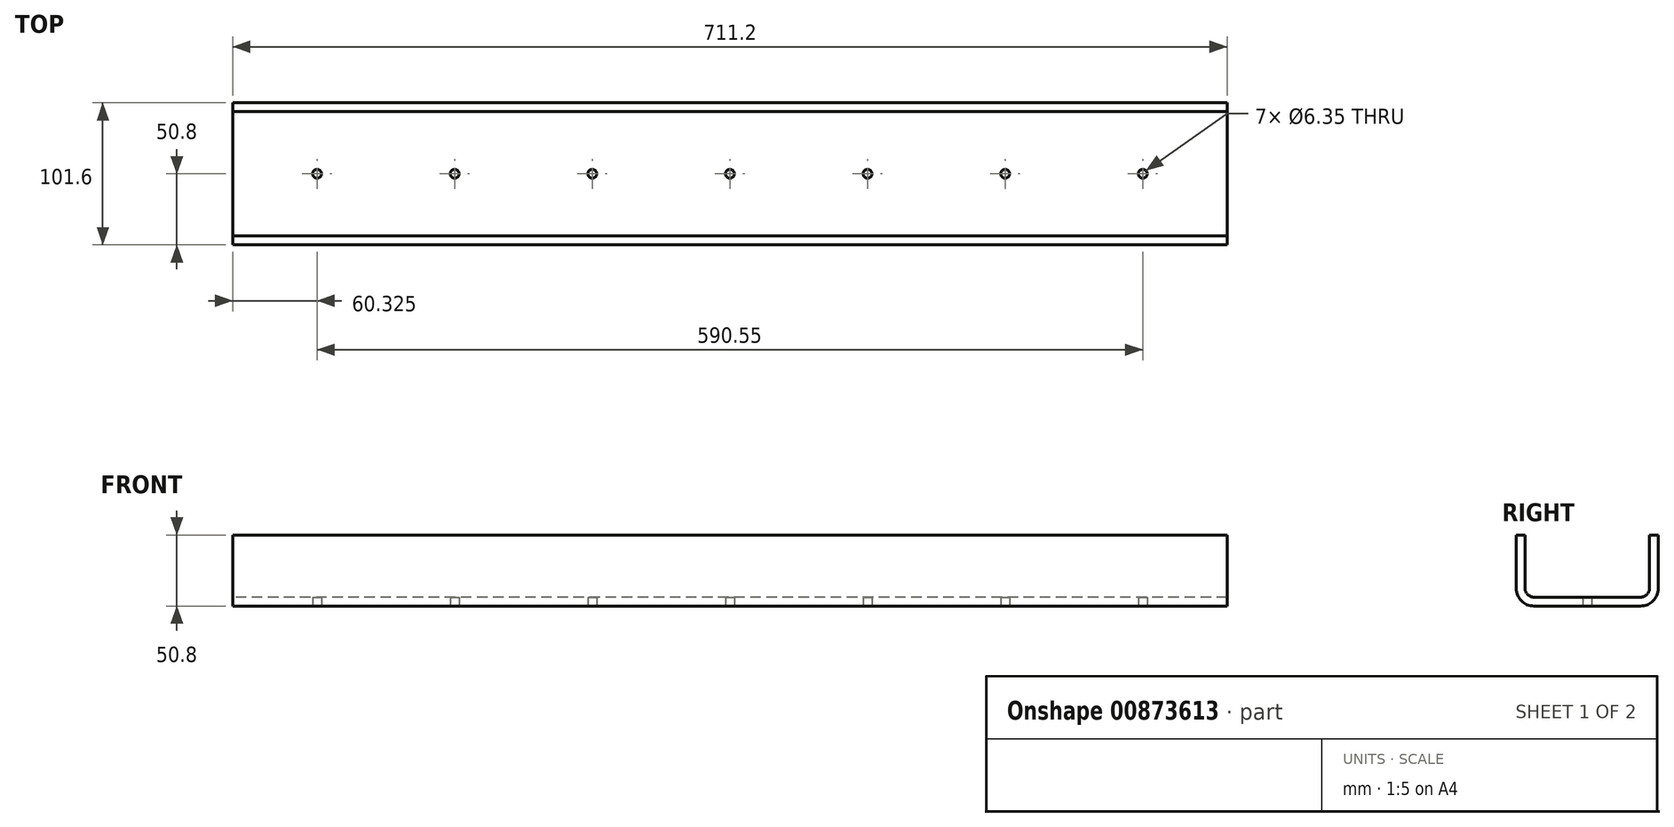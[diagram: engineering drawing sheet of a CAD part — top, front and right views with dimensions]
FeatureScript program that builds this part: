
annotation { "Feature Type Name" : "Feature", "Feature Type Description" : "" }
export const myFeature = defineFeature(function(context is Context, id is Id, definition is map)
    precondition{}
    {
        {
            var Q0;
            Q0=qCreatedBy(makeId("Right.planeOp"),FACE);
            var sketch = newSketch(context, id + "F0", { "sketchPlane" : qUnion([Q0])});
            skLineSegment(sketch, "E0.top", {"start": v(38.1, -25.4) * mm, "end": v(-38.1, -25.4) * mm});
            skLineSegment(sketch, "E0.left", {"start": v(50.8, 25.4) * mm, "end": v(50.8, -12.7) * mm});
            skLineSegment(sketch, "E0.right", {"start": v(-50.8, 25.4) * mm, "end": v(-50.8, -12.7) * mm});
            skPoint(sketch, "E0.middle", {"position": v(0, 0) * mm});
            skPoint(sketch, "E1.visualSharp", {"position": v(-50.8, -25.4) * mm});
            skArc(sketch, "E1.filletArc", {"start": v(-50.8, -12.7) * mm, "mid": v(-47.08, -21.68) * mm, "end": v(-38.1, -25.4) * mm});
            skPoint(sketch, "E2.visualSharp", {"position": v(50.8, -25.4) * mm});
            skArc(sketch, "E2.filletArc", {"start": v(38.1, -25.4) * mm, "mid": v(47.08, -21.68) * mm, "end": v(50.8, -12.7) * mm});
            skLineSegment(sketch, "E3.0", {"start": v(-44.45, 25.4) * mm, "end": v(-44.45, -12.7) * mm});
            skLineSegment(sketch, "E3.1", {"start": v(38.1, -19.05) * mm, "end": v(-38.1, -19.05) * mm});
            skLineSegment(sketch, "E3.2", {"start": v(44.45, 25.4) * mm, "end": v(44.45, -12.7) * mm});
            skLineSegment(sketch, "E4", {"start": v(-50.8, 25.4) * mm, "end": v(-44.45, 25.4) * mm});
            skLineSegment(sketch, "E5", {"start": v(44.45, 25.4) * mm, "end": v(50.8, 25.4) * mm});
            skPoint(sketch, "E6.visualSharp", {"position": v(-44.45, -19.05) * mm});
            skArc(sketch, "E6.filletArc", {"start": v(-44.45, -12.7) * mm, "mid": v(-42.6, -17.2) * mm, "end": v(-38.1, -19.05) * mm});
            skPoint(sketch, "E7.visualSharp", {"position": v(44.45, -19.05) * mm});
            skArc(sketch, "E7.filletArc", {"start": v(38.1, -19.05) * mm, "mid": v(42.6, -17.2) * mm, "end": v(44.45, -12.7) * mm});
            skSolve(sketch);
        }
        {
            var Q0;
            Q0 = qSketchRegion(id + "F0", true);
            extrude(context, id + "F1", {"entities" : qUnion([Q0]), "depth" : 711.2 * mm, "offsetDistance" : 25.4 * mm});
        }
        {
            var Q0;
            Q0=makeQuery(id+"F1.opExtrude","SWEPT_FACE",FACE,{"disambiguationData":[OSD([sQuery(id+"F0.wireOp",EDGE,"E0.top")])]});
            var sketch = newSketch(context, id + "F2", { "sketchPlane" : qUnion([Q0])});
            skCircle(sketch, "E8", {"center": v(355.6, 0) * mm, "radius": 3.18 * mm});
            skPoint(sketch, "E8.centerSnap0", {"position": v(355.6, -38.1) * mm});
            skCircle(sketch, "E9.1.0.0", {"center": v(454.03, 0) * mm, "radius": 3.18 * mm});
            skCircle(sketch, "E9.2.0.0", {"center": v(552.45, 0) * mm, "radius": 3.18 * mm});
            skCircle(sketch, "E9.3.0.0", {"center": v(650.88, 0) * mm, "radius": 3.18 * mm});
            skLineSegment(sketch, "E9.direction1", {"start": v(355.6, 0) * mm, "end": v(454.03, 0) * mm, "construction": true});
            skCircle(sketch, "E10.1.0.0", {"center": v(257.18, 0) * mm, "radius": 3.18 * mm});
            skCircle(sketch, "E10.2.0.0", {"center": v(158.75, 0) * mm, "radius": 3.18 * mm});
            skCircle(sketch, "E10.3.0.0", {"center": v(60.32, 0) * mm, "radius": 3.18 * mm});
            skLineSegment(sketch, "E10.direction1", {"start": v(355.6, 0) * mm, "end": v(257.18, 0) * mm, "construction": true});
            skSolve(sketch);
        }
        {
            var Q0;
            Q0 = qSketchRegion(id + "F2", true);
            extrude(context, id + "F3", {"entities" : qUnion([Q0]), "operationType" : NewBodyOperationType.REMOVE, "oppositeDirection" : true, "depth" : 25.4 * mm, "offsetDistance" : 25.4 * mm});
        }
    });
